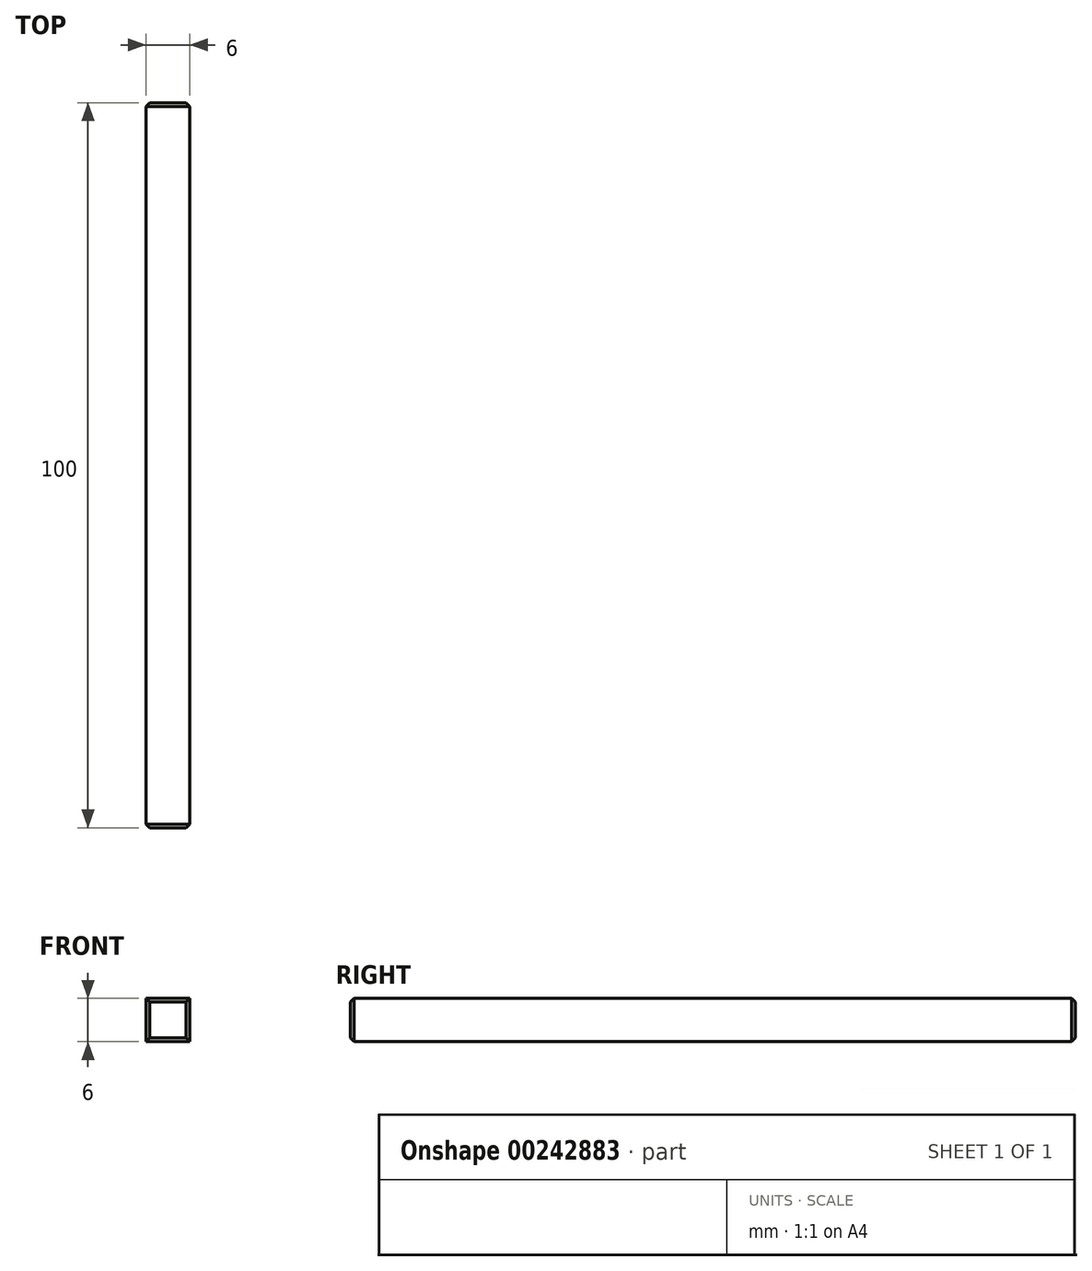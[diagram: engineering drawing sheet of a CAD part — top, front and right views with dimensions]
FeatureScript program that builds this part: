
annotation { "Feature Type Name" : "Feature", "Feature Type Description" : "" }
export const myFeature = defineFeature(function(context is Context, id is Id, definition is map)
    precondition{}
    {
        {
            assignVariable(context, id + "F0", {"name" : "Length", "anyValue" : 100});
        }
        {
            var Q0;
            Q0=qCreatedBy(makeId("Front.planeOp"),FACE);
            var sketch = newSketch(context, id + "F1", { "sketchPlane" : qUnion([Q0])});
            skLineSegment(sketch, "E0.bottom", {"start": v(3, 3) * mm, "end": v(-3, 3) * mm});
            skLineSegment(sketch, "E0.top", {"start": v(3, -3) * mm, "end": v(-3, -3) * mm});
            skLineSegment(sketch, "E0.left", {"start": v(3, 3) * mm, "end": v(3, -3) * mm});
            skLineSegment(sketch, "E0.right", {"start": v(-3, 3) * mm, "end": v(-3, -3) * mm});
            skPoint(sketch, "E0.middle", {"position": v(0, 0) * mm});
            skSolve(sketch);
        }
        {
            var Q0;
            Q0=makeQuery(id+"F1.imprint","IMPRINT",FACE,{"disambiguationData":[TD([[makeQuery(id+"F1.imprint","IMPRINT",EDGE,{"derivedFrom":sQuery(id+"F1.wireOp",EDGE,"E0.bottom")}),1.0]])]});
            extrude(context, id + "F2", {"entities" : qUnion([Q0]), "depth" : (getVariable(context, 'Length')) * mm});
        }
        {
            var Q0;
            Q0=makeQuery(id+"F2.opExtrude","CAP_EDGE",EDGE,{"disambiguationData":[OSD([sQuery(id+"F1.wireOp",EDGE,"E0.bottom")])],"isStart":false});
            var Q1;
            Q1=makeQuery(id+"F2.opExtrude","CAP_EDGE",EDGE,{"disambiguationData":[OSD([sQuery(id+"F1.wireOp",EDGE,"E0.left")])],"isStart":false});
            var Q2;
            Q2=makeQuery(id+"F2.opExtrude","CAP_EDGE",EDGE,{"disambiguationData":[OSD([sQuery(id+"F1.wireOp",EDGE,"E0.top")])],"isStart":false});
            var Q3;
            Q3=makeQuery(id+"F2.opExtrude","CAP_EDGE",EDGE,{"disambiguationData":[OSD([sQuery(id+"F1.wireOp",EDGE,"E0.right")])],"isStart":false});
            var Q4;
            Q4=makeQuery(id+"F2.opExtrude","CAP_EDGE",EDGE,{"disambiguationData":[OSD([sQuery(id+"F1.wireOp",EDGE,"E0.bottom")])],"isStart":true});
            var Q5;
            Q5=makeQuery(id+"F2.opExtrude","CAP_EDGE",EDGE,{"disambiguationData":[OSD([sQuery(id+"F1.wireOp",EDGE,"E0.right")])],"isStart":true});
            var Q6;
            Q6=makeQuery(id+"F2.opExtrude","CAP_EDGE",EDGE,{"disambiguationData":[OSD([sQuery(id+"F1.wireOp",EDGE,"E0.top")])],"isStart":true});
            var Q7;
            Q7=makeQuery(id+"F2.opExtrude","CAP_EDGE",EDGE,{"disambiguationData":[OSD([sQuery(id+"F1.wireOp",EDGE,"E0.left")])],"isStart":true});
            chamfer(context, id + "F3", {"entities" : qUnion([Q0, Q1, Q2, Q3, Q4, Q5, Q6, Q7]), "width" : 0.5 * mm, "tangentPropagation" : true});
        }
    });
